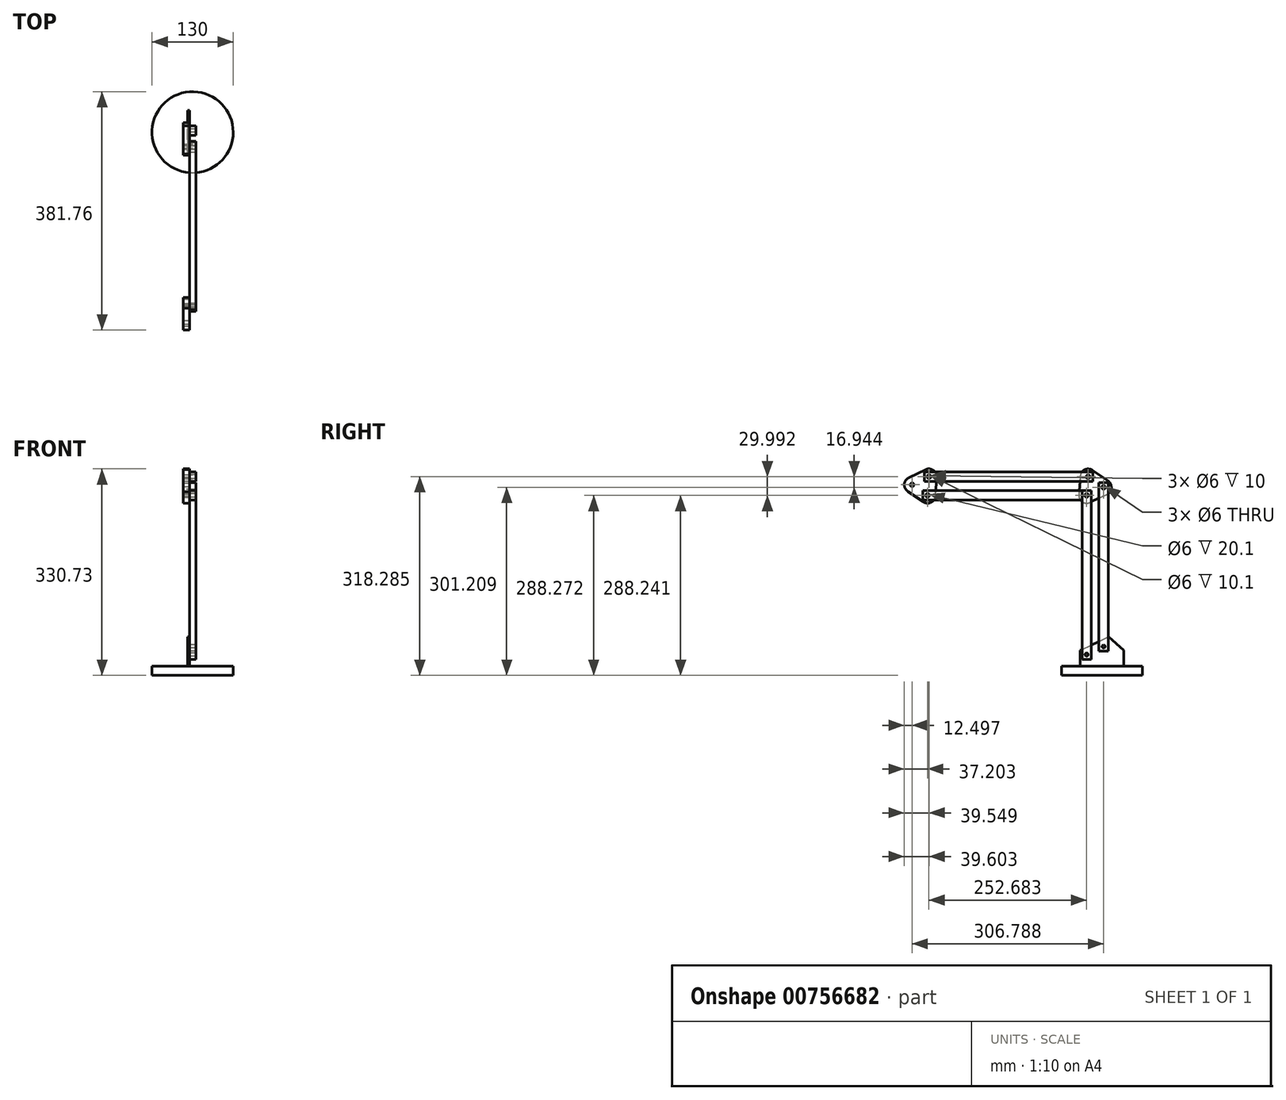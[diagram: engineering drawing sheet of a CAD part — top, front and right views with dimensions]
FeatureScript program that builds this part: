
annotation { "Feature Type Name" : "Feature", "Feature Type Description" : "" }
export const myFeature = defineFeature(function(context is Context, id is Id, definition is map)
    precondition{}
    {
        {
            var Q0;
            Q0=qCreatedBy(makeId("Top.planeOp"),FACE);
            var sketch = newSketch(context, id + "F0", { "sketchPlane" : qUnion([Q0])});
            skCircle(sketch, "E0", {"center": v(0, 0) * mm, "radius": 65 * mm});
            skSolve(sketch);
        }
        {
            var Q0;
            Q0 = qSketchRegion(id + "F0", true);
            extrude(context, id + "F1", {"entities" : qUnion([Q0]), "depth" : 15 * mm, "offsetDistance" : 25 * mm});
        }
        {
            var Q0;
            Q0=makeQuery(id+"F1.opExtrude","CAP_FACE",FACE,{"disambiguationData":[OSD([sQuery(id+"F0.wireOp",EDGE,"E0")])],"isStart":false});
            var sketch = newSketch(context, id + "F2", { "sketchPlane" : qUnion([Q0])});
            skLineSegment(sketch, "E1", {"start": v(-5, 35) * mm, "end": v(-8, 35) * mm});
            skLineSegment(sketch, "E2", {"start": v(-8, 35) * mm, "end": v(-8, -35) * mm});
            skLineSegment(sketch, "E3", {"start": v(-5, -35) * mm, "end": v(-8, -35) * mm});
            skLineSegment(sketch, "E4", {"start": v(-5, 35) * mm, "end": v(-5, -35) * mm});
            skPoint(sketch, "E5.start.orphan", {"position": v(5, 0) * mm});
            skPoint(sketch, "E6.center.orphan", {"position": v(0, 0) * mm});
            skSolve(sketch);
        }
        {
            var Q0;
            Q0 = qSketchRegion(id + "F2", true);
            extrude(context, id + "F3", {"entities" : qUnion([Q0]), "operationType" : NewBodyOperationType.ADD, "depth" : 25 * mm, "offsetDistance" : 25 * mm});
        }
        {
            var Q0;
            Q0=makeQuery(id+"F3.opExtrude","SWEPT_FACE",FACE,{"disambiguationData":[OSD([sQuery(id+"F2.wireOp",EDGE,"E2")])]});
            var sketch = newSketch(context, id + "F4", { "sketchPlane" : qUnion([Q0])});
            skLineSegment(sketch, "E7", {"start": v(35, 40) * mm, "end": v(-10.64, 61.75) * mm});
            skLineSegment(sketch, "E8", {"start": v(-35, 40) * mm, "end": v(-10.64, 61.75) * mm});
            skLineSegment(sketch, "E9", {"start": v(-35, 40) * mm, "end": v(35, 40) * mm});
            skSolve(sketch);
        }
        {
            var Q0;
            Q0 = qSketchRegion(id + "F4", true);
            extrude(context, id + "F5", {"entities" : qUnion([Q0]), "operationType" : NewBodyOperationType.ADD, "oppositeDirection" : true, "depth" : 3 * mm, "offsetDistance" : 25 * mm});
        }
        {
            var Q0;
            Q0=makeQuery(id+"F5.boolean.opBoolean","MERGE",FACE,{"derivedFrom":[makeQuery(id+"F3.opExtrude","SWEPT_FACE",FACE,{"disambiguationData":[OSD([sQuery(id+"F2.wireOp",EDGE,"E2")])]}),makeQuery(id+"F5.opExtrude","CAP_FACE",FACE,{"disambiguationData":[OSD([sQuery(id+"F4.wireOp",EDGE,"E7"),sQuery(id+"F4.wireOp",EDGE,"E8"),sQuery(id+"F4.wireOp",EDGE,"E9")])],"isStart":true})]});
            var sketch = newSketch(context, id + "F6", { "sketchPlane" : qUnion([Q0])});
            skPoint(sketch, "E10.startSnap0", {"position": v(24.56, 33.3) * mm});
            skCircle(sketch, "E11", {"center": v(24.56, 33.3) * mm, "radius": 3 * mm});
            skCircle(sketch, "E12", {"center": v(-2.53, 46.2) * mm, "radius": 3 * mm});
            skPoint(sketch, "E13.orphan", {"position": v(-19.16, 54.14) * mm});
            skPoint(sketch, "E14.orphan", {"position": v(14.11, 38.28) * mm});
            skPoint(sketch, "E15.orphan", {"position": v(35, 28.33) * mm});
            skPoint(sketch, "E16.orphan", {"position": v(35, 33.3) * mm});
            skSolve(sketch);
        }
        {
            var Q0;
            Q0=sQuery(id+"F6.wireOp",VERTEX,"E12.center");
            var Q1;
            Q1=sQuery(id+"F6.wireOp",VERTEX,"E10.startSnap0");
            var Q2;
            Q2=makeQuery(id+"F1.opExtrude","SWEPT_BODY",BODY,{"disambiguationData":[OSD([sQuery(id+"F0.wireOp",EDGE,"E0")])]});
            hole(context, id + "F7", {"style" : HoleStyle.SIMPLE, "endStyle" : HoleEndStyle.THROUGH, "holeDiameter" : 5 * mm, "majorDiameter" : 5 * mm, "isTappedThrough" : true, "tappedDepth" : 12 * mm, "tapClearance" : 3, "locations" : qUnion([Q0, Q1]), "scope" : qUnion([Q2])});
        }
        {
            var Q0;
            Q0=makeQuery(id+"F5.boolean.opBoolean","MERGE",FACE,{"derivedFrom":[makeQuery(id+"F3.opExtrude","SWEPT_FACE",FACE,{"disambiguationData":[OSD([sQuery(id+"F2.wireOp",EDGE,"E4")])]}),makeQuery(id+"F5.opExtrude","CAP_FACE",FACE,{"disambiguationData":[OSD([sQuery(id+"F4.wireOp",EDGE,"E7"),sQuery(id+"F4.wireOp",EDGE,"E8"),sQuery(id+"F4.wireOp",EDGE,"E9")])],"isStart":false})]});
            var sketch = newSketch(context, id + "F8", { "sketchPlane" : qUnion([Q0])});
            skLineSegment(sketch, "E17", {"start": v(-32.06, 25.8) * mm, "end": v(-17.06, 25.8) * mm});
            skPoint(sketch, "E18.start.orphan", {"position": v(-24.56, 33.3) * mm});
            skPoint(sketch, "E19.start.orphan", {"position": v(-32.06, 33.3) * mm});
            skLineSegment(sketch, "E20", {"start": v(-32.06, 25.8) * mm, "end": v(-32.06, 295.8) * mm});
            skLineSegment(sketch, "E21", {"start": v(-17.06, 25.8) * mm, "end": v(-17.06, 295.8) * mm});
            skLineSegment(sketch, "E22", {"start": v(-32.06, 295.8) * mm, "end": v(-17.06, 295.8) * mm});
            skLineSegment(sketch, "E23", {"start": v(10.03, 38.7) * mm, "end": v(-4.97, 38.7) * mm});
            skLineSegment(sketch, "E24", {"start": v(-4.97, 38.7) * mm, "end": v(-4.97, 308.7) * mm});
            skPoint(sketch, "E25.start.orphan", {"position": v(2.53, 46.2) * mm});
            skLineSegment(sketch, "E26", {"start": v(10.03, 38.7) * mm, "end": v(10.03, 308.7) * mm});
            skLineSegment(sketch, "E27", {"start": v(-4.97, 308.7) * mm, "end": v(10.03, 308.7) * mm});
            skCircle(sketch, "E28", {"center": v(-24.56, 288.3) * mm, "radius": 3 * mm});
            skPoint(sketch, "E29.orphan", {"position": v(-24.56, 295.8) * mm});
            skLineSegment(sketch, "E30", {"start": v(2.53, 308.7) * mm, "end": v(2.53, 301.2) * mm});
            skCircle(sketch, "E31", {"center": v(2.53, 301.2) * mm, "radius": 3 * mm});
            skSolve(sketch);
        }
        {
            var Q0;
            {var subQ0=sQuery(id+"F8.wireOp",EDGE,"E22");Q0=makeQuery(id+"F8.imprint","IMPRINT",FACE,{"disambiguationData":[TD([[makeQuery(id+"F8.imprint","IMPRINT",EDGE,{"derivedFrom":subQ0}),-1.0]])]});}
            var Q1;
            Q1=makeQuery(id+"F8.imprint","IMPRINT",FACE,{"disambiguationData":[TD([[makeQuery(id+"F8.imprint","IMPRINT",EDGE,{"derivedFrom":sQuery(id+"F8.wireOp",EDGE,"E31")}),-1.0]])]});
            var Q2;
            {var subQ2=sQuery(id+"F8.wireOp",EDGE,"E23");Q2=makeQuery(id+"F8.imprint","IMPRINT",FACE,{"disambiguationData":[TD([[makeQuery(id+"F8.imprint","IMPRINT",EDGE,{"derivedFrom":subQ2}),-1.0]])]});}
            var Q3;
            {var subQ1=sQuery(id+"F8.wireOp",EDGE,"E17");Q3=makeQuery(id+"F8.imprint","IMPRINT",FACE,{"disambiguationData":[TD([[makeQuery(id+"F8.imprint","IMPRINT",EDGE,{"derivedFrom":subQ1}),1.0]])]});}
            extrude(context, id + "F9", {"entities" : qUnion([Q0, Q1, Q2, Q3]), "operationType" : NewBodyOperationType.ADD, "depth" : 10 * mm, "offsetDistance" : 25 * mm});
        }
        {
            var Q0;
            Q0=makeQuery(id+"F9.opExtrude","CAP_FACE",FACE,{"disambiguationData":[OSD([sQuery(id+"F2.wireOp",EDGE,"E4"),sQuery(id+"F4.wireOp",EDGE,"E7"),sQuery(id+"F4.wireOp",EDGE,"E8"),sQuery(id+"F4.wireOp",EDGE,"E9"),sQuery(id+"F7.hole-0.sketch.wireOp",EDGE,"core_line_2"),sQuery(id+"F8.wireOp",EDGE,"E23"),sQuery(id+"F8.wireOp",EDGE,"E24"),sQuery(id+"F8.wireOp",EDGE,"E26"),sQuery(id+"F8.wireOp",EDGE,"E27"),sQuery(id+"F8.wireOp",EDGE,"E31")])],"isStart":true});
            var sketch = newSketch(context, id + "F10", { "sketchPlane" : qUnion([Q0])});
            skArc(sketch, "E32", {"start": v(34.73, 317.89) * mm, "mid": v(28.18, 329.15) * mm, "end": v(15.16, 328.46) * mm});
            skArc(sketch, "E33", {"start": v(-8.9, 311.96) * mm, "mid": v(-15.01, 300.65) * mm, "end": v(-7.93, 289.94) * mm});
            skArc(sketch, "E34", {"start": v(18.95, 277.05) * mm, "mid": v(31.52, 277.88) * mm, "end": v(36.99, 289.22) * mm});
            skLineSegment(sketch, "E35", {"start": v(-10.25, 311.03) * mm, "end": v(15.16, 328.46) * mm});
            skLineSegment(sketch, "E36", {"start": v(34.73, 317.89) * mm, "end": v(36.99, 289.22) * mm});
            skLineSegment(sketch, "E37", {"start": v(19.3, 276.89) * mm, "end": v(-7.93, 289.94) * mm});
            skCircle(sketch, "E38", {"center": v(22.23, 318.15) * mm, "radius": 3 * mm});
            skCircle(sketch, "E39", {"center": v(24.53, 288.24) * mm, "radius": 3 * mm});
            skCircle(sketch, "E40", {"center": v(-2.53, 301.2) * mm, "radius": 3 * mm});
            skSolve(sketch);
        }
        {
            var Q0;
            {var subQ12=sQuery(id+"F10.wireOp",EDGE,"E32");Q0=makeQuery(id+"F10.imprint","IMPRINT",FACE,{"disambiguationData":[TD([[makeQuery(id+"F10.imprint","IMPRINT",EDGE,{"derivedFrom":subQ12}),1.0]])]});}
            var Q1;
            Q1=makeQuery(id+"F10.imprint","IMPRINT",FACE,{"disambiguationData":[TD([[makeQuery(id+"F10.imprint","IMPRINT",EDGE,{"derivedFrom":sQuery(id+"F10.wireOp",EDGE,"E40")}),1.0]])]});
            extrude(context, id + "F11", {"entities" : qUnion([Q0, Q1]), "operationType" : NewBodyOperationType.ADD, "depth" : 10 * mm, "offsetDistance" : 25 * mm});
        }
        {
            var Q0;
            {var subQ0=sQuery(id+"F10.wireOp",EDGE,"E33");var subQ10=sQuery(id+"F8.wireOp",EDGE,"E20");var subQ11=sQuery(id+"F10.wireOp",EDGE,"E32");var subQ12=sQuery(id+"F10.wireOp",EDGE,"E34");var subQ13=sQuery(id+"F10.wireOp",EDGE,"E35");var subQ14=sQuery(id+"F10.wireOp",EDGE,"E36");var subQ15=sQuery(id+"F10.wireOp",EDGE,"E37");var subQ16=sQuery(id+"F10.wireOp",EDGE,"E38");Q0=makeQuery(id+"F11.boolean.opBoolean","SPLIT",FACE,{"disambiguationData":[TD([makeQuery(id+"F9.opExtrude","SWEPT_FACE",FACE,{"disambiguationData":[OSD([subQ10])]})])],"derivedFrom":makeQuery(id+"F11.opExtrude","CAP_FACE",FACE,{"disambiguationData":[OSD([subQ11,subQ0,subQ12,subQ13,subQ14,subQ15,subQ16,sQuery(id+"F10.wireOp",EDGE,"E39"),sQuery(id+"F10.wireOp",EDGE,"E40")])],"isStart":true})});}
            var sketch = newSketch(context, id + "F12", { "sketchPlane" : qUnion([Q0])});
            skPoint(sketch, "E41.endSnap0", {"position": v(-51.05, 310.86) * mm});
            skLineSegment(sketch, "E42", {"start": v(-17.06, 280.74) * mm, "end": v(-287.06, 280.74) * mm});
            skPoint(sketch, "E43.end.orphan", {"position": v(-24.53, 280.74) * mm});
            skPoint(sketch, "E43.start.orphan", {"position": v(-24.53, 288.24) * mm});
            skLineSegment(sketch, "E44", {"start": v(-17.06, 280.74) * mm, "end": v(-17.06, 295.8) * mm});
            skLineSegment(sketch, "E45", {"start": v(-17.06, 295.8) * mm, "end": v(-287.06, 295.8) * mm});
            skLineSegment(sketch, "E46", {"start": v(-287.06, 295.8) * mm, "end": v(-287.06, 280.74) * mm});
            skPoint(sketch, "E47.start.orphan", {"position": v(-22.23, 318.15) * mm});
            skLineSegment(sketch, "E48", {"start": v(-14.66, 310.75) * mm, "end": v(-284.66, 310.75) * mm});
            skLineSegment(sketch, "E49", {"start": v(-14.66, 310.75) * mm, "end": v(-14.66, 325.82) * mm});
            skLineSegment(sketch, "E50", {"start": v(-14.66, 325.82) * mm, "end": v(-284.66, 325.82) * mm});
            skLineSegment(sketch, "E51", {"start": v(-284.66, 325.82) * mm, "end": v(-284.66, 310.75) * mm});
            skCircle(sketch, "E52", {"center": v(-22.23, 318.15) * mm, "radius": 3 * mm});
            skCircle(sketch, "E53", {"center": v(-24.53, 288.24) * mm, "radius": 3 * mm});
            skCircle(sketch, "E54", {"center": v(-277.16, 318.29) * mm, "radius": 3 * mm});
            skCircle(sketch, "E55", {"center": v(-279.56, 288.27) * mm, "radius": 3 * mm});
            skPoint(sketch, "E56.start.orphan", {"position": v(-284.66, 318.29) * mm});
            skPoint(sketch, "E57.orphan", {"position": v(-287.06, 288.27) * mm});
            skSolve(sketch);
        }
        {
            var Q0;
            {var subQ0=sQuery(id+"F12.wireOp",EDGE,"E46");Q0=makeQuery(id+"F12.imprint","IMPRINT",FACE,{"disambiguationData":[TD([[makeQuery(id+"F12.imprint","IMPRINT",EDGE,{"derivedFrom":subQ0}),1.0]])]});}
            var Q1;
            {var subQ5=sQuery(id+"F12.wireOp",EDGE,"E51");Q1=makeQuery(id+"F12.imprint","IMPRINT",FACE,{"disambiguationData":[TD([[makeQuery(id+"F12.imprint","IMPRINT",EDGE,{"derivedFrom":subQ5}),1.0]])]});}
            var Q2;
            {var subQ0=sQuery(id+"F10.wireOp",EDGE,"E36");var subQ4=makeQuery(id+"F11.opExtrude","CAP_EDGE",EDGE,{"disambiguationData":[OSD([subQ0])],"isStart":true});var subQ6=sQuery(id+"F12.wireOp",EDGE,"E45");var subQ7=makeQuery(id+"F12.imprint","INTERSECT",VERTEX,{"derivedFrom":[subQ4,subQ6]});Q2=makeQuery(id+"F12.imprint","IMPRINT",FACE,{"disambiguationData":[TD([[makeQuery(id+"F12.imprint","IMPRINT",EDGE,{"disambiguationData":[TD([[subQ7,-1.0]])],"derivedFrom":subQ4}),1.0]])]});}
            var Q3;
            {var subQ1=sQuery(id+"F12.wireOp",EDGE,"E49");Q3=makeQuery(id+"F12.imprint","IMPRINT",FACE,{"disambiguationData":[TD([[makeQuery(id+"F12.imprint","IMPRINT",EDGE,{"derivedFrom":subQ1}),1.0]])]});}
            extrude(context, id + "F13", {"entities" : qUnion([Q0, Q1, Q2, Q3]), "operationType" : NewBodyOperationType.ADD, "depth" : 10.1 * mm, "offsetDistance" : 25 * mm});
        }
        {
            var Q0;
            Q0=makeQuery(id+"F13.opExtrude","CAP_FACE",FACE,{"disambiguationData":[OSD([sQuery(id+"F8.wireOp",EDGE,"E20"),sQuery(id+"F12.wireOp",EDGE,"E42"),sQuery(id+"F12.wireOp",EDGE,"E45"),sQuery(id+"F12.wireOp",EDGE,"E46"),sQuery(id+"F12.wireOp",EDGE,"E55")])],"isStart":true});
            var sketch = newSketch(context, id + "F14", { "sketchPlane" : qUnion([Q0])});
            skArc(sketch, "E58", {"start": v(310.28, 294.3) * mm, "mid": v(316.76, 305.62) * mm, "end": v(309.66, 316.54) * mm});
            skArc(sketch, "E59", {"start": v(283.33, 329.13) * mm, "mid": v(270.49, 328.77) * mm, "end": v(264.75, 317.28) * mm});
            skArc(sketch, "E60", {"start": v(267.03, 287.55) * mm, "mid": v(274.03, 277.08) * mm, "end": v(286.59, 278.02) * mm});
            skLineSegment(sketch, "E61", {"start": v(281.86, 329.84) * mm, "end": v(309.66, 316.54) * mm});
            skLineSegment(sketch, "E62", {"start": v(310.28, 294.3) * mm, "end": v(286.59, 278.02) * mm});
            skLineSegment(sketch, "E63", {"start": v(267.06, 287.17) * mm, "end": v(264.75, 317.28) * mm});
            skCircle(sketch, "E64", {"center": v(304.26, 305.27) * mm, "radius": 3 * mm});
            skCircle(sketch, "E65", {"center": v(279.5, 288.32) * mm, "radius": 3 * mm});
            skCircle(sketch, "E66", {"center": v(277.21, 318.23) * mm, "radius": 3 * mm});
            skSolve(sketch);
        }
        {
            var Q0;
            {var subQ12=sQuery(id+"F12.wireOp",EDGE,"E46");var subQ13=makeQuery(id+"F13.opExtrude","CAP_EDGE",EDGE,{"disambiguationData":[OSD([subQ12])],"isStart":true});Q0=makeQuery(id+"F14.imprint","IMPRINT",FACE,{"disambiguationData":[TD([[makeQuery(id+"F14.imprint","IMPRINT",EDGE,{"derivedFrom":subQ13}),-1.0]])]});}
            var Q1;
            {var subQ2=sQuery(id+"F14.wireOp",EDGE,"E58");Q1=makeQuery(id+"F14.imprint","IMPRINT",FACE,{"disambiguationData":[TD([[makeQuery(id+"F14.imprint","IMPRINT",EDGE,{"derivedFrom":subQ2}),1.0]])]});}
            extrude(context, id + "F15", {"entities" : qUnion([Q0, Q1]), "operationType" : NewBodyOperationType.ADD, "depth" : 10 * mm, "offsetDistance" : 25 * mm});
        }
    });
